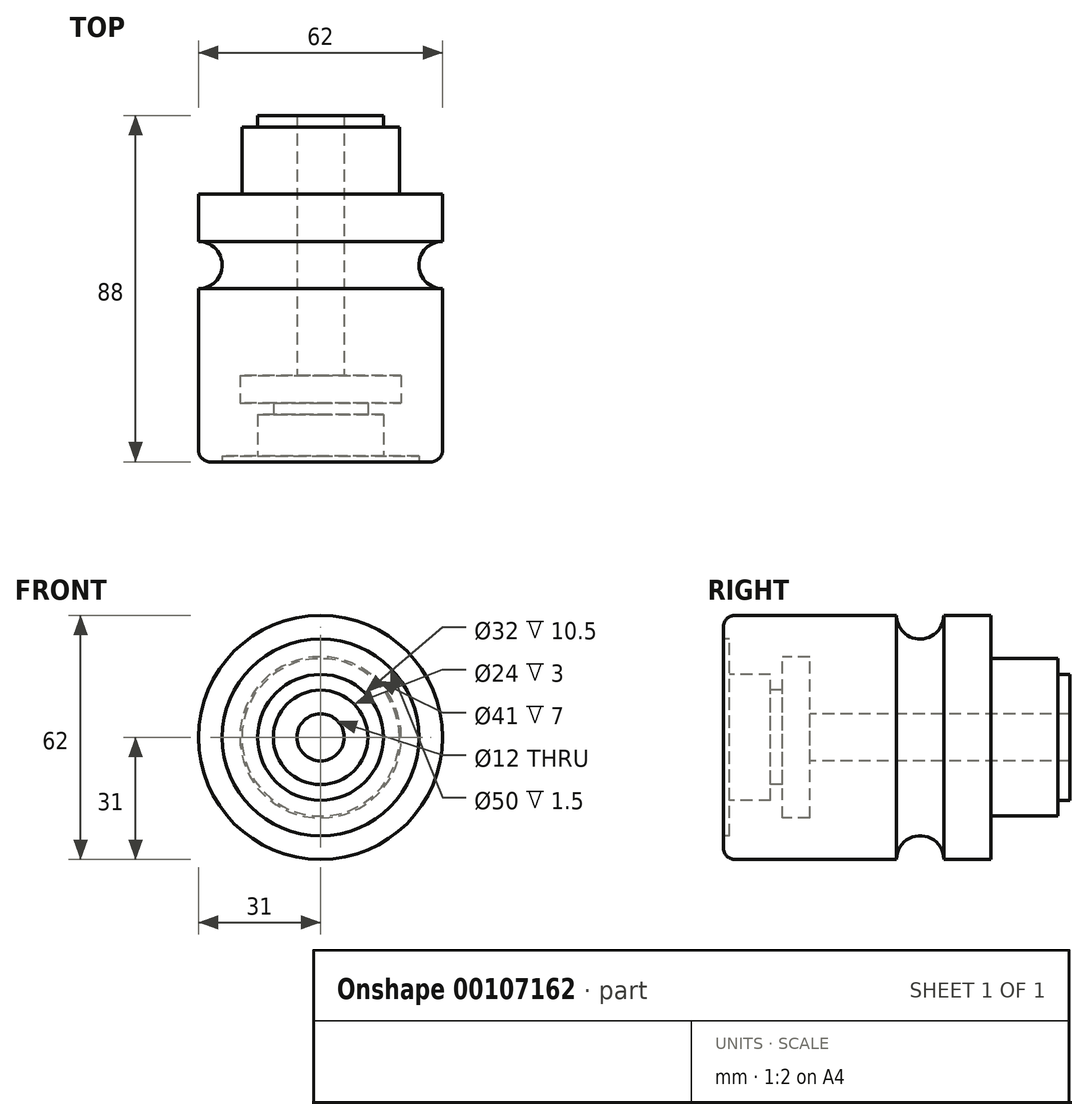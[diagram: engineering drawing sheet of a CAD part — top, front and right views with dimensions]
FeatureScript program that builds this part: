
annotation { "Feature Type Name" : "Feature", "Feature Type Description" : "" }
export const myFeature = defineFeature(function(context is Context, id is Id, definition is map)
    precondition{}
    {
        {
            var Q0;
            Q0=qCreatedBy(makeId("Right.planeOp"),FACE);
            var sketch = newSketch(context, id + "F0", { "sketchPlane" : qUnion([Q0])});
            skLineSegment(sketch, "E0", {"start": v(0, 0) * mm, "end": v(88, 0) * mm, "construction": true});
            skLineSegment(sketch, "E1", {"start": v(88, 0) * mm, "end": v(88, 6) * mm, "construction": true});
            skLineSegment(sketch, "E2", {"start": v(88, 0) * mm, "end": v(88, 16) * mm, "construction": true});
            skLineSegment(sketch, "E3", {"start": v(88, 0) * mm, "end": v(85, 0) * mm, "construction": true});
            skLineSegment(sketch, "E4", {"start": v(85, 0) * mm, "end": v(85, 20) * mm, "construction": true});
            skLineSegment(sketch, "E5", {"start": v(0, 0) * mm, "end": v(0, 31) * mm});
            skLineSegment(sketch, "E6", {"start": v(0, 31) * mm, "end": v(44, 31) * mm});
            skLineSegment(sketch, "E7", {"start": v(44, 31) * mm, "end": v(50, 31) * mm, "construction": true});
            skCircle(sketch, "E8", {"center": v(50, 31) * mm, "radius": 6 * mm});
            skLineSegment(sketch, "E9", {"start": v(50, 31) * mm, "end": v(56, 31) * mm, "construction": true});
            skLineSegment(sketch, "E10", {"start": v(56, 31) * mm, "end": v(68, 31) * mm});
            skLineSegment(sketch, "E11", {"start": v(85, 20) * mm, "end": v(68, 20) * mm});
            skLineSegment(sketch, "E12", {"start": v(68, 31) * mm, "end": v(68, 20) * mm});
            skLineSegment(sketch, "E13", {"start": v(88, 0) * mm, "end": v(88, 16) * mm});
            skLineSegment(sketch, "E14", {"start": v(88, 16) * mm, "end": v(85, 16) * mm});
            skLineSegment(sketch, "E15", {"start": v(85, 16) * mm, "end": v(85, 20) * mm});
            skLineSegment(sketch, "E16", {"start": v(0, 0) * mm, "end": v(0, 25) * mm, "construction": true});
            skLineSegment(sketch, "E17", {"start": v(0, 25) * mm, "end": v(1.5, 25) * mm});
            skLineSegment(sketch, "E18", {"start": v(1.5, 25) * mm, "end": v(1.5, 16) * mm});
            skLineSegment(sketch, "E19", {"start": v(1.5, 16) * mm, "end": v(12, 16) * mm});
            skLineSegment(sketch, "E20", {"start": v(12, 16) * mm, "end": v(12, 12) * mm});
            skLineSegment(sketch, "E21", {"start": v(12, 12) * mm, "end": v(15, 12) * mm});
            skLineSegment(sketch, "E22", {"start": v(15, 12) * mm, "end": v(15, 0) * mm, "construction": true});
            skLineSegment(sketch, "E23", {"start": v(15, 0) * mm, "end": v(15, 20.5) * mm, "construction": true});
            skLineSegment(sketch, "E24", {"start": v(15, 12) * mm, "end": v(15, 20.5) * mm});
            skLineSegment(sketch, "E25", {"start": v(15, 20.5) * mm, "end": v(0, 20.5) * mm, "construction": true});
            skPoint(sketch, "E25.endSnap0", {"position": v(1.5, 20.5) * mm});
            skLineSegment(sketch, "E26", {"start": v(0, 20.5) * mm, "end": v(22, 20.5) * mm, "construction": true});
            skLineSegment(sketch, "E27", {"start": v(15, 20.5) * mm, "end": v(22, 20.5) * mm});
            skLineSegment(sketch, "E28", {"start": v(22, 20.5) * mm, "end": v(22, 0) * mm, "construction": true});
            skLineSegment(sketch, "E29", {"start": v(22, 0) * mm, "end": v(22, 6) * mm, "construction": true});
            skLineSegment(sketch, "E30", {"start": v(22, 20.5) * mm, "end": v(22, 6) * mm});
            skLineSegment(sketch, "E31", {"start": v(22, 6) * mm, "end": v(88, 6) * mm});
            skSolve(sketch);
        }
        {
            var Q0;
            {var subQ3=sQuery(id+"F0.wireOp",EDGE,"E6");Q0=makeQuery(id+"F0.imprint","IMPRINT",FACE,{"disambiguationData":[TD([[makeQuery(id+"F0.imprint","IMPRINT",EDGE,{"derivedFrom":subQ3}),-1.0]])]});}
            var Q1;
            Q1=sQuery(id+"F0.wireOp",EDGE,"E0");
            revolve(context, id + "F1", {"entities" : qUnion([Q0]), "axis" : qUnion([Q1]), "revolveType" : RevolveType.FULL});
        }
        {
            var Q0;
            Q0=makeQuery(id+"F1.opRevolve","SWEPT_EDGE",EDGE,{"disambiguationData":[OSD([sQuery(id+"F0.wireOp",EDGE,"E5"),sQuery(id+"F0.wireOp",EDGE,"E6")])]});
            fillet(context, id + "F2", {"entities" : qUnion([Q0]), "radius" : 3 * mm, "tangentPropagation" : true, "allowEdgeOverflow" : false});
        }
    });
